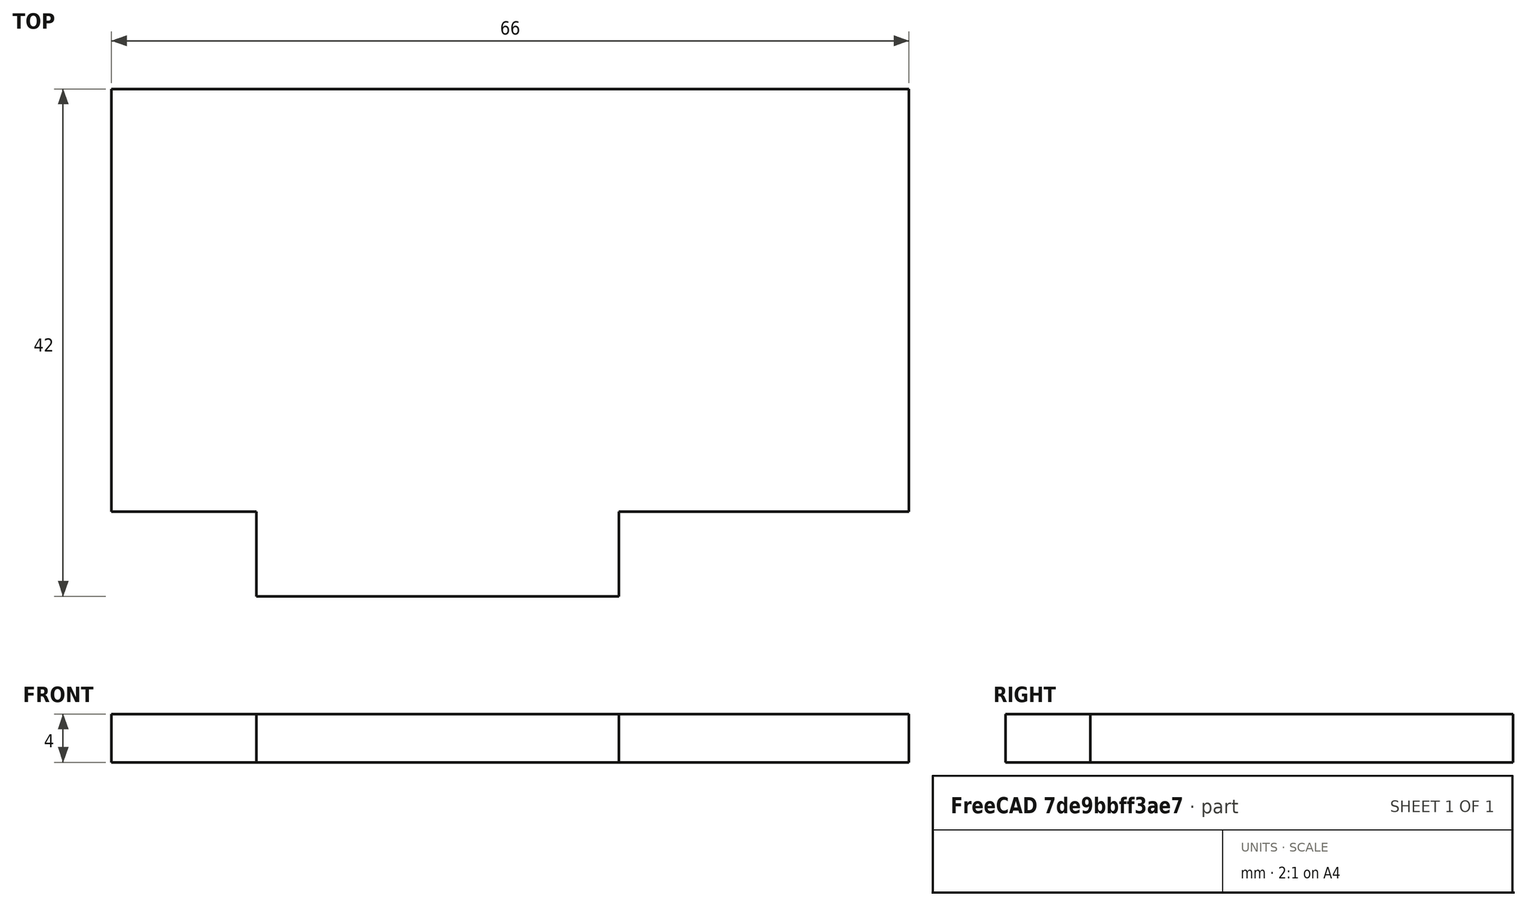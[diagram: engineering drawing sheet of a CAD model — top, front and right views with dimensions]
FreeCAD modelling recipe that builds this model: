
FCSTD DOCUMENT  (FreeCAD 0.18R4 (GitTag))
Label: Balance board plate
License: All rights reserved
LicenseURL: http://en.wikipedia.org/wiki/All_rights_reserved
objects: Sketcher::SketchObject×1, PartDesign::Pad×1, PartDesign::Body×1
note: 4 computed .brp shape members not serialized (recipe doc carries the construction recipe); baked Part::Feature solids carry a one-line shape summary decoded from their .brp

FEATURE [Sketcher::SketchObject] Sketch
  MapMode = 5
  Support = -> [XY_Plane]
  sketch-geometry (8):
    g0: LineSegment StartX=0 StartY=0 StartZ=0 EndX=12 EndY=0 EndZ=0
    g1: LineSegment StartX=0 StartY=0 StartZ=0 EndX=0 EndY=35 EndZ=0
    g2: LineSegment StartX=12 StartY=0 StartZ=0 EndX=12 EndY=-7 EndZ=0
    g3: LineSegment StartX=12 StartY=-7 StartZ=0 EndX=42 EndY=-7 EndZ=0
    g4: LineSegment StartX=42 StartY=-7 StartZ=0 EndX=42 EndY=0 EndZ=0
    g5: LineSegment StartX=42 StartY=0 StartZ=0 EndX=66 EndY=0 EndZ=0
    g6: LineSegment StartX=66 StartY=0 StartZ=0 EndX=66 EndY=35 EndZ=0
    g7: LineSegment StartX=0 StartY=35 StartZ=0 EndX=66 EndY=35 EndZ=0
  constraints (23):
    c: DistanceX(g0,g0) = 12
    c: Coincident(g0,g-1)
    c: Horizontal(g0)
    c: Coincident(g0,g1)
    c: Vertical(g1)
    c: DistanceY(g1,g1) = 35
    c: Vertical(g2)
    c: Coincident(g0,g2)
    c: DistanceY(g2,g2) = 7
    c: Coincident(g2,g3)
    c: Horizontal(g3)
    c: DistanceX(g3,g3) = 30
    c: Coincident(g3,g4)
    c: Vertical(g4)
    c: DistanceY(g4,g4) = 7
    c: Coincident(g4,g5)
    c: Horizontal(g5)
    c: DistanceX(g5,g5) = 24
    c: Coincident(g5,g6)
    c: Vertical(g6)
    c: DistanceY(g6,g6) = 35
    c: Coincident(g1,g7)
    c: Coincident(g6,g7)
FEATURE [PartDesign::Pad] Pad
  Length = 4
  Length2 = 100
  Profile = -> Sketch
  Type = 0
FEATURE [PartDesign::Body] Body
  Group = -> [Sketch,Pad]
  Origin = -> Origin
  Tip = -> Pad
